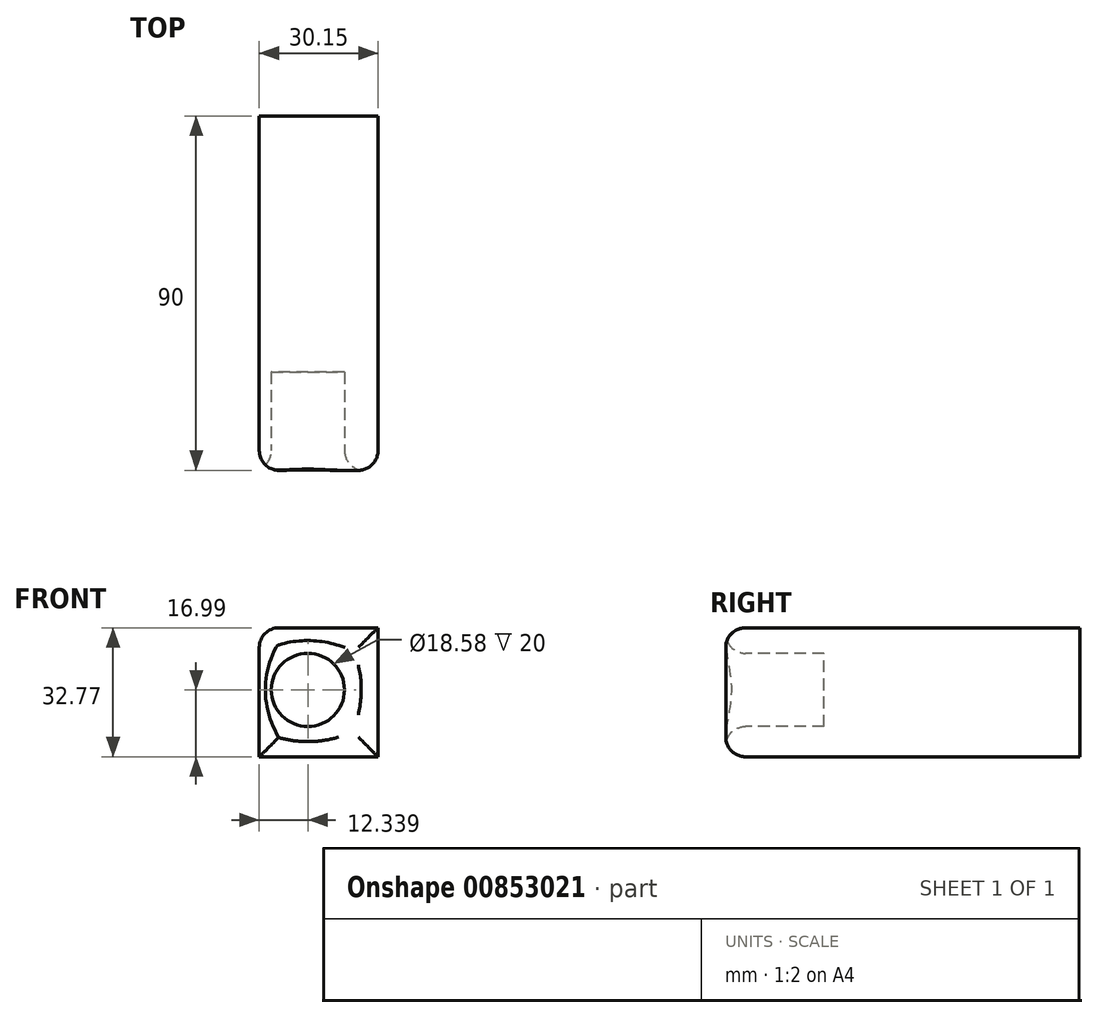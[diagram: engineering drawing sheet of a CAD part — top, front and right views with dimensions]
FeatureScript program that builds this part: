
annotation { "Feature Type Name" : "Feature", "Feature Type Description" : "" }
export const myFeature = defineFeature(function(context is Context, id is Id, definition is map)
    precondition{}
    {
        {
            var Q0;
            Q0=qCreatedBy(makeId("Front.planeOp"),FACE);
            var sketch = newSketch(context, id + "F0", { "sketchPlane" : qUnion([Q0])});
            skLineSegment(sketch, "E0.bottom", {"start": v(0, 0) * mm, "end": v(30.15, 0) * mm});
            skLineSegment(sketch, "E0.top", {"start": v(0, 32.77) * mm, "end": v(30.15, 32.77) * mm});
            skLineSegment(sketch, "E0.left", {"start": v(0, 0) * mm, "end": v(0, 32.77) * mm});
            skLineSegment(sketch, "E0.right", {"start": v(30.15, 0) * mm, "end": v(30.15, 32.77) * mm});
            skSolve(sketch);
        }
        {
            var Q0;
            Q0 = qSketchRegion(id + "F0", true);
            extrude(context, id + "F1", {"entities" : qUnion([Q0]), "depth" : 90 * mm, "offsetDistance" : 25 * mm});
        }
        {
            var Q0;
            Q0=makeQuery(id+"F1.opExtrude","CAP_FACE",FACE,{"disambiguationData":[OSD([sQuery(id+"F0.wireOp",EDGE,"E0.bottom"),sQuery(id+"F0.wireOp",EDGE,"E0.top"),sQuery(id+"F0.wireOp",EDGE,"E0.left"),sQuery(id+"F0.wireOp",EDGE,"E0.right")])],"isStart":false});
            var sketch = newSketch(context, id + "F2", { "sketchPlane" : qUnion([Q0])});
            skCircle(sketch, "E1", {"center": v(12.34, 16.99) * mm, "radius": 9.3 * mm});
            skSolve(sketch);
        }
        {
            var Q0;
            Q0 = qSketchRegion(id + "F2", true);
            extrude(context, id + "F3", {"entities" : qUnion([Q0]), "operationType" : NewBodyOperationType.REMOVE, "oppositeDirection" : true, "depth" : 25 * mm, "offsetDistance" : 25 * mm});
        }
        {
            var Q0;
            Q0=makeQuery(id+"F1.opExtrude","CAP_FACE",FACE,{"disambiguationData":[OSD([sQuery(id+"F0.wireOp",EDGE,"E0.bottom"),sQuery(id+"F0.wireOp",EDGE,"E0.top"),sQuery(id+"F0.wireOp",EDGE,"E0.left"),sQuery(id+"F0.wireOp",EDGE,"E0.right")])],"isStart":false});
            fillet(context, id + "F4", {"entities" : qUnion([Q0]), "radius" : 5 * mm, "tangentPropagation" : true, "allowEdgeOverflow" : false});
        }
        {
            var Q0;
            Q0=makeQuery(id+"F1.opExtrude","SWEPT_EDGE",EDGE,{"disambiguationData":[OSD([sQuery(id+"F0.wireOp",EDGE,"E0.top"),sQuery(id+"F0.wireOp",EDGE,"E0.left")])]});
            fillet(context, id + "F5", {"entities" : qUnion([Q0]), "radius" : 5 * mm, "tangentPropagation" : true, "allowEdgeOverflow" : false});
        }
    });
